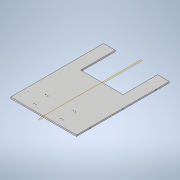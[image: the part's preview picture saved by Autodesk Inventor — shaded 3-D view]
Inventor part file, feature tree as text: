
AUTODESK INVENTOR PART (.ipt)
format: ipt  version: 2021 (Build 250183000, 183)  size: 186,880 bytes
history: native  units: in
note: dims shown in document units (in); Inventor stores cm internally (conversion verified against a paired STEP export)
features: sketch x7, extrude x6, other x1, hole x1, plane x1, mirror x1
ambient origin geometry x8: Origin, YZ Plane, XZ Plane, XY Plane, X Axis, Y Axis, Z Axis, Center Point
bodies: Solid1 (feature_tree)
feature tree (17):
  other  "main plate"
  extrude  "Extrusion1"  Depth=17.5in
  extrude  "Extrusion2"  Depth=0.25in
  extrude  "Extrusion3"  Depth=3.746in
  extrude  "Extrusion4"  Depth=1.185in
  extrude  "Extrusion5"  Depth=0.107in
  hole  "Hole1"  [1 undecoded]
  plane  "Work Plane1"
  mirror  "Mirror1"
  extrude  "Extrusion6"  Depth=2.2in
  sketch  "Sketch1"  dims[d0=12.4in d1=17.5in]
  sketch  "Sketch2"  dims[d2=0.25in d3=0.0in d4=0.107in]
  sketch  "Sketch3"  dims[d5=0.107in d7=3.746in]
  sketch  "Sketch4"  dims[d8=0.394in d9=1.185in]
  sketch  "Sketch5"  dims[d10=1.0in d11=0.0in d12=0.107in]
  sketch  "Sketch6"  dims[d13=0.107in d14=2.482in]
  sketch  "Sketch7"  dims[d15=2.482in d16=0.394in d17=3.846in d18=1.0in d19=0.0in d20=0.107in d21=0.107in d22=0.394in d23=2.929in d24=3.665in d25=1.0in d26=0.0in d27=0.107in d28=0.107in d31=1.13in d32=0.394in d34=1.0in d35=0.0in d36=8.741in d37=1.185in d38=1.13in d39=0.25in d40=0.125in d41=0.125in d42=0.125in d43=2.5in d44=2.5in d45=12.5in d46=6.25in d47=0.196in d48=0.5in d49=0.375in d50=0.25in d51=0.5635in d52=0.75in d53=0.8108in d54=8.0in d55=6.5in d56=2.2in d57=0.0in d58=0.0in]
note: 1 required parameter value undecoded (feature->parameter linkage not recoverable at this tier; creation-order binding heuristic only, values carry confidence <= 0.55)
